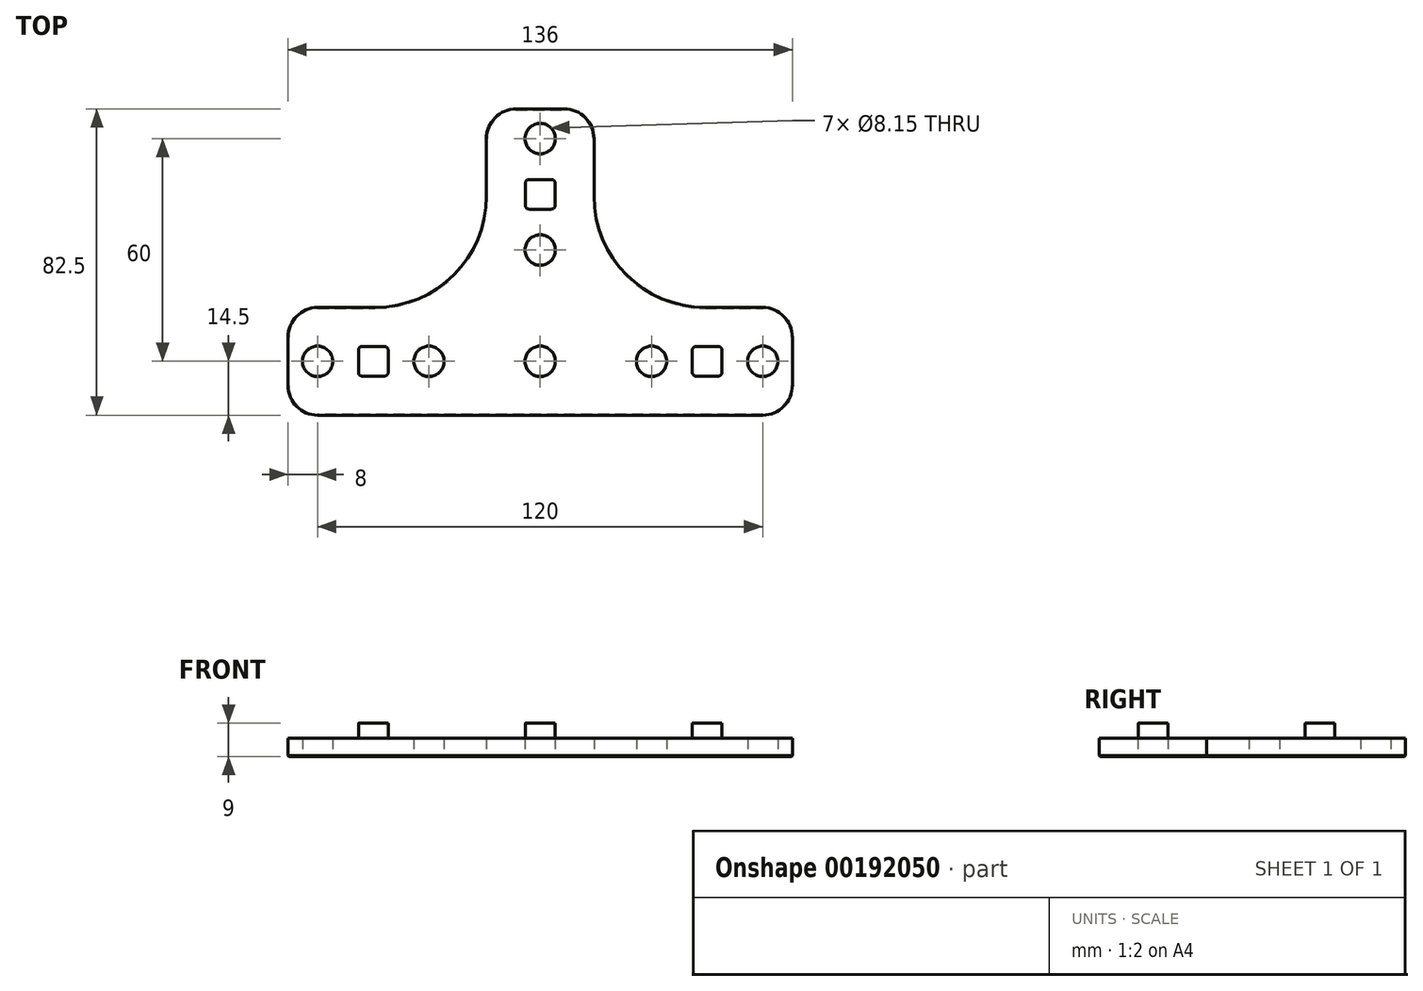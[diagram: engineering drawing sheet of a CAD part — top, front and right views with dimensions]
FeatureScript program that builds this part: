
annotation { "Feature Type Name" : "Feature", "Feature Type Description" : "" }
export const myFeature = defineFeature(function(context is Context, id is Id, definition is map)
    precondition{}
    {
        {
            var Q0;
            Q0=qCreatedBy(makeId("Top.planeOp"),FACE);
            var sketch = newSketch(context, id + "F0", { "sketchPlane" : qUnion([Q0])});
            skCircle(sketch, "E0", {"center": v(-60, 0) * mm, "radius": 4.08 * mm});
            skCircle(sketch, "E1", {"center": v(-30, 0) * mm, "radius": 4.08 * mm});
            skCircle(sketch, "E2", {"center": v(0, 0) * mm, "radius": 4.08 * mm});
            skLineSegment(sketch, "E3", {"start": v(-68, 14.5) * mm, "end": v(-68, -14.5) * mm});
            skLineSegment(sketch, "E4", {"start": v(-68, -14.5) * mm, "end": v(0, -14.5) * mm});
            skLineSegment(sketch, "E5", {"start": v(-68, 14.5) * mm, "end": v(-14.5, 14.5) * mm});
            skCircle(sketch, "E6.1.0", {"center": v(0, 60) * mm, "radius": 4.08 * mm});
            skCircle(sketch, "E6.1.1", {"center": v(0, 30) * mm, "radius": 4.08 * mm});
            skLineSegment(sketch, "E6.1.3", {"start": v(14.5, 68) * mm, "end": v(14.5, 14.5) * mm});
            skLineSegment(sketch, "E6.1.4", {"start": v(14.5, 68) * mm, "end": v(-14.5, 68) * mm});
            skLineSegment(sketch, "E6.1.5", {"start": v(-14.5, 68) * mm, "end": v(-14.5, 14.5) * mm});
            skCircle(sketch, "E6.2.0", {"center": v(60, 0) * mm, "radius": 4.08 * mm});
            skCircle(sketch, "E6.2.1", {"center": v(30, 0) * mm, "radius": 4.08 * mm});
            skLineSegment(sketch, "E6.2.3", {"start": v(68, -14.5) * mm, "end": v(0, -14.5) * mm});
            skLineSegment(sketch, "E6.2.4", {"start": v(68, -14.5) * mm, "end": v(68, 14.5) * mm});
            skLineSegment(sketch, "E6.2.5", {"start": v(68, 14.5) * mm, "end": v(14.5, 14.5) * mm});
            skLineSegment(sketch, "E6.anchor1", {"start": v(0, 0) * mm, "end": v(-60, 0) * mm, "construction": true});
            skLineSegment(sketch, "E6.anchor2", {"start": v(0, 0) * mm, "end": v(60, 0) * mm, "construction": true});
            skPoint(sketch, "E7.orphan", {"position": v(0, 14.5) * mm});
            skPoint(sketch, "E8.orphan", {"position": v(14.5, 0) * mm});
            skPoint(sketch, "E9.orphan", {"position": v(-14.5, 0) * mm});
            skSolve(sketch);
        }
        {
            var Q0;
            Q0 = qSketchRegion(id + "F0", true);
            extrude(context, id + "F1", {"entities" : qUnion([Q0]), "depth" : 5 * mm});
        }
        {
            var Q0;
            Q0=makeQuery(id+"F1.opExtrude","SWEPT_EDGE",EDGE,{"disambiguationData":[OSD([sQuery(id+"F0.wireOp",EDGE,"E6.1.4"),sQuery(id+"F0.wireOp",EDGE,"E6.1.5")])]});
            var Q1;
            Q1=makeQuery(id+"F1.opExtrude","SWEPT_EDGE",EDGE,{"disambiguationData":[OSD([sQuery(id+"F0.wireOp",EDGE,"E6.1.3"),sQuery(id+"F0.wireOp",EDGE,"E6.1.4")])]});
            var Q2;
            Q2=makeQuery(id+"F1.opExtrude","SWEPT_EDGE",EDGE,{"disambiguationData":[OSD([sQuery(id+"F0.wireOp",EDGE,"E3"),sQuery(id+"F0.wireOp",EDGE,"E5")])]});
            var Q3;
            Q3=makeQuery(id+"F1.opExtrude","SWEPT_EDGE",EDGE,{"disambiguationData":[OSD([sQuery(id+"F0.wireOp",EDGE,"E3"),sQuery(id+"F0.wireOp",EDGE,"E4")])]});
            var Q4;
            Q4=makeQuery(id+"F1.opExtrude","SWEPT_EDGE",EDGE,{"disambiguationData":[OSD([sQuery(id+"F0.wireOp",EDGE,"E6.2.4"),sQuery(id+"F0.wireOp",EDGE,"E6.2.5")])]});
            var Q5;
            Q5=makeQuery(id+"F1.opExtrude","SWEPT_EDGE",EDGE,{"disambiguationData":[OSD([sQuery(id+"F0.wireOp",EDGE,"E6.2.3"),sQuery(id+"F0.wireOp",EDGE,"E6.2.4")])]});
            fillet(context, id + "F2", {"entities" : qUnion([Q0, Q1, Q2, Q3, Q4, Q5]), "radius" : 8 * mm, "allowEdgeOverflow" : false});
        }
        {
            var Q0;
            Q0=makeQuery(id+"F1.opExtrude","SWEPT_EDGE",EDGE,{"disambiguationData":[OSD([sQuery(id+"F0.wireOp",EDGE,"E6.1.3"),sQuery(id+"F0.wireOp",EDGE,"E6.2.5")])]});
            var Q1;
            Q1=makeQuery(id+"F1.opExtrude","SWEPT_EDGE",EDGE,{"disambiguationData":[OSD([sQuery(id+"F0.wireOp",EDGE,"E5"),sQuery(id+"F0.wireOp",EDGE,"E6.1.5")])]});
            fillet(context, id + "F3", {"entities" : qUnion([Q0, Q1]), "radius" : 30 * mm, "allowEdgeOverflow" : false});
        }
        {
            var Q0;
            Q0=makeQuery(id+"F1.opExtrude","CAP_FACE",FACE,{"disambiguationData":[OSD([sQuery(id+"F0.wireOp",EDGE,"E0"),sQuery(id+"F0.wireOp",EDGE,"E1"),sQuery(id+"F0.wireOp",EDGE,"E3"),sQuery(id+"F0.wireOp",EDGE,"E4"),sQuery(id+"F0.wireOp",EDGE,"E5"),sQuery(id+"F0.wireOp",EDGE,"E6.1.0"),sQuery(id+"F0.wireOp",EDGE,"E6.1.1"),sQuery(id+"F0.wireOp",EDGE,"E6.1.3"),sQuery(id+"F0.wireOp",EDGE,"E6.1.4"),sQuery(id+"F0.wireOp",EDGE,"E6.1.5"),sQuery(id+"F0.wireOp",EDGE,"E6.2.0"),sQuery(id+"F0.wireOp",EDGE,"E6.2.1"),sQuery(id+"F0.wireOp",EDGE,"E2"),sQuery(id+"F0.wireOp",EDGE,"E6.2.3"),sQuery(id+"F0.wireOp",EDGE,"E6.2.4"),sQuery(id+"F0.wireOp",EDGE,"E6.2.5")])],"isStart":false});
            var sketch = newSketch(context, id + "F4", { "sketchPlane" : qUnion([Q0])});
            skCircle(sketch, "E10.0", {"center": v(-60, 0) * mm, "radius": 4.08 * mm, "construction": true});
            skCircle(sketch, "E11.0", {"center": v(-30, 0) * mm, "radius": 4.08 * mm, "construction": true});
            skCircle(sketch, "E12.0", {"center": v(0, 30) * mm, "radius": 4.08 * mm, "construction": true});
            skCircle(sketch, "E13.0", {"center": v(0, 60) * mm, "radius": 4.08 * mm, "construction": true});
            skCircle(sketch, "E14.0", {"center": v(30, 0) * mm, "radius": 4.08 * mm, "construction": true});
            skCircle(sketch, "E15.0", {"center": v(60, 0) * mm, "radius": 4.08 * mm, "construction": true});
            skLineSegment(sketch, "E16", {"start": v(0, 60) * mm, "end": v(0, 30) * mm, "construction": true});
            skLineSegment(sketch, "E17", {"start": v(-60, 0) * mm, "end": v(-30, 0) * mm, "construction": true});
            skLineSegment(sketch, "E18", {"start": v(60, 0) * mm, "end": v(30, 0) * mm, "construction": true});
            skLineSegment(sketch, "E19.bottom", {"start": v(-41, 4) * mm, "end": v(-49, 4) * mm});
            skLineSegment(sketch, "E19.top", {"start": v(-41, -4) * mm, "end": v(-49, -4) * mm});
            skLineSegment(sketch, "E19.left", {"start": v(-41, 4) * mm, "end": v(-41, -4) * mm});
            skLineSegment(sketch, "E19.right", {"start": v(-49, 4) * mm, "end": v(-49, -4) * mm});
            skPoint(sketch, "E19.middle", {"position": v(-45, 0) * mm});
            skPoint(sketch, "E20.center", {"position": v(0, 0) * mm});
            skSolve(sketch);
        }
        {
            var Q0;
            Q0 = qSketchRegion(id + "F4", true);
            extrude(context, id + "F5", {"entities" : qUnion([Q0]), "depth" : 4 * mm});
        }
        {
            var Q0;
            Q0=makeQuery(id+"F5.opExtrude","SWEPT_EDGE",EDGE,{"disambiguationData":[OSD([sQuery(id+"F4.wireOp",EDGE,"E19.top"),sQuery(id+"F4.wireOp",EDGE,"E19.right")])]});
            var Q1;
            Q1=makeQuery(id+"F5.opExtrude","SWEPT_EDGE",EDGE,{"disambiguationData":[OSD([sQuery(id+"F4.wireOp",EDGE,"E19.top"),sQuery(id+"F4.wireOp",EDGE,"E19.left")])]});
            var Q2;
            Q2=makeQuery(id+"F5.opExtrude","SWEPT_EDGE",EDGE,{"disambiguationData":[OSD([sQuery(id+"F4.wireOp",EDGE,"E19.bottom"),sQuery(id+"F4.wireOp",EDGE,"E19.right")])]});
            var Q3;
            Q3=makeQuery(id+"F5.opExtrude","SWEPT_EDGE",EDGE,{"disambiguationData":[OSD([sQuery(id+"F4.wireOp",EDGE,"E19.bottom"),sQuery(id+"F4.wireOp",EDGE,"E19.left")])]});
            fillet(context, id + "F6", {"entities" : qUnion([Q0, Q1, Q2, Q3]), "radius" : 1 * mm, "allowEdgeOverflow" : false});
        }
        {
            var Q0;
            Q0=qCreatedBy(makeId("Front.planeOp"),FACE);
            var sketch = newSketch(context, id + "F7", { "sketchPlane" : qUnion([Q0])});
            skLineSegment(sketch, "E21", {"start": v(0, 0) * mm, "end": v(0, 22.7) * mm});
            skSolve(sketch);
        }
        {
            var Q0;
            Q0=makeQuery(id+"F5.opExtrude","SWEPT_BODY",BODY,{"disambiguationData":[OSD([sQuery(id+"F4.wireOp",EDGE,"E19.bottom"),sQuery(id+"F4.wireOp",EDGE,"E19.top"),sQuery(id+"F4.wireOp",EDGE,"E19.left"),sQuery(id+"F4.wireOp",EDGE,"E19.right")])]});
            var Q1;
            Q1=sQuery(id+"F7.wireOp",EDGE,"E21");
            circularPattern(context, id + "F8", {"operationType" : NewBodyOperationType.ADD, "entities" : qUnion([Q0]), "axis" : qUnion([Q1]), "angle" : 180 * degree, "instanceCount" : 3, "oppositeDirection" : true, "equalSpace" : true});
        }
        {
            var Q0;
            Q0=makeQuery(id+"F1.opExtrude","CAP_FACE",FACE,{"disambiguationData":[OSD([sQuery(id+"F0.wireOp",EDGE,"E0"),sQuery(id+"F0.wireOp",EDGE,"E1"),sQuery(id+"F0.wireOp",EDGE,"E3"),sQuery(id+"F0.wireOp",EDGE,"E4"),sQuery(id+"F0.wireOp",EDGE,"E5"),sQuery(id+"F0.wireOp",EDGE,"E6.1.0"),sQuery(id+"F0.wireOp",EDGE,"E6.1.1"),sQuery(id+"F0.wireOp",EDGE,"E6.1.3"),sQuery(id+"F0.wireOp",EDGE,"E6.1.4"),sQuery(id+"F0.wireOp",EDGE,"E6.1.5"),sQuery(id+"F0.wireOp",EDGE,"E6.2.0"),sQuery(id+"F0.wireOp",EDGE,"E6.2.1"),sQuery(id+"F0.wireOp",EDGE,"E2"),sQuery(id+"F0.wireOp",EDGE,"E6.2.3"),sQuery(id+"F0.wireOp",EDGE,"E6.2.4"),sQuery(id+"F0.wireOp",EDGE,"E6.2.5")])],"isStart":true});
            chamfer(context, id + "F9", {"entities" : qUnion([Q0]), "width" : 0.25 * mm});
        }
    });
